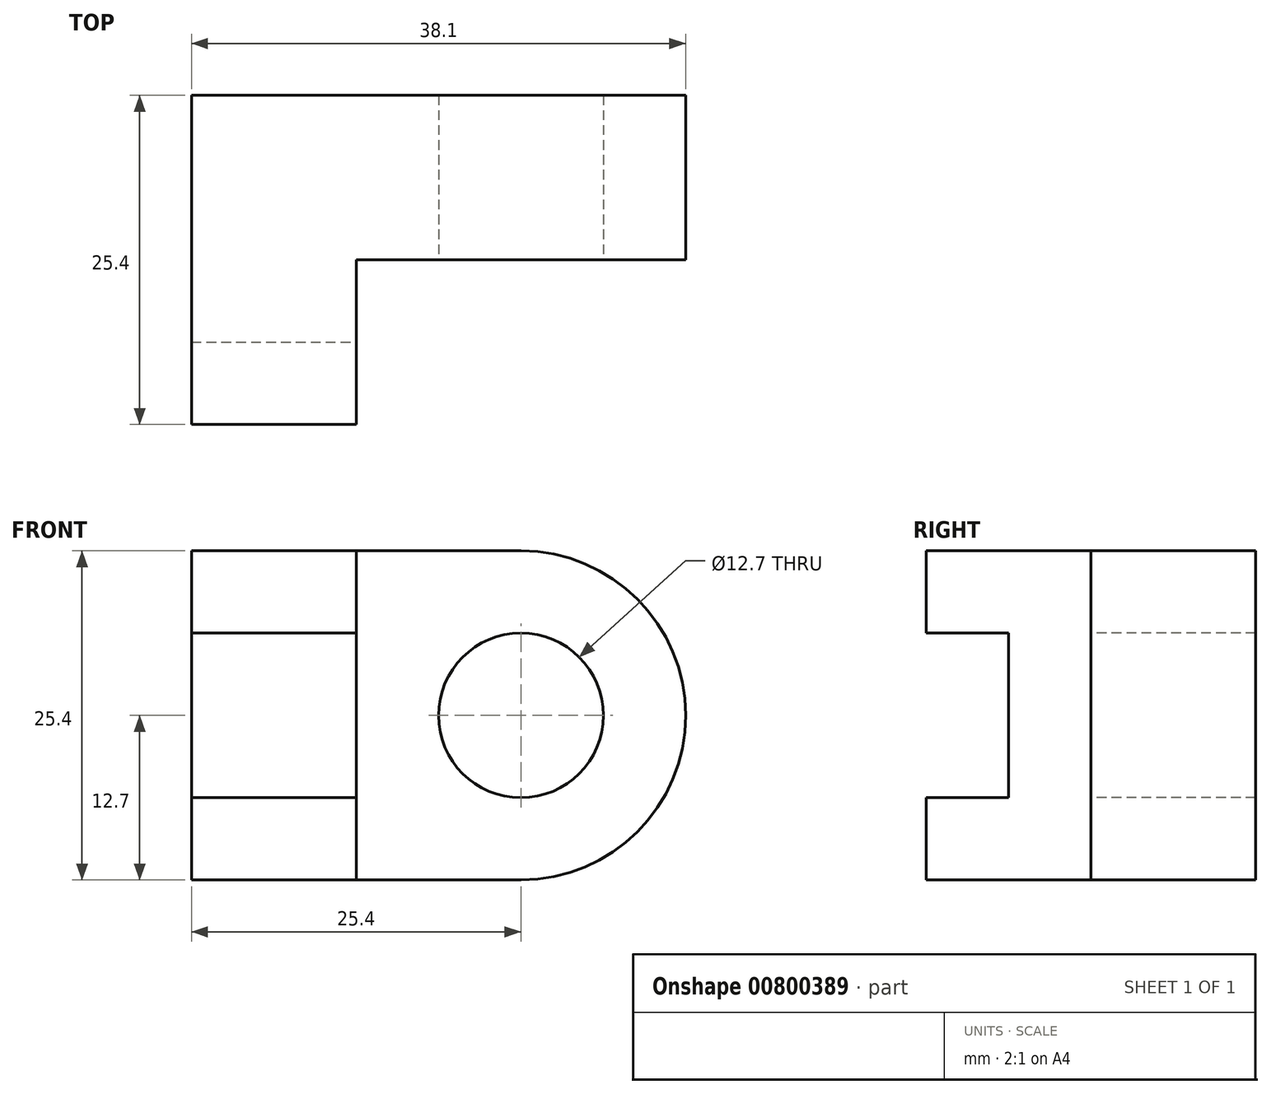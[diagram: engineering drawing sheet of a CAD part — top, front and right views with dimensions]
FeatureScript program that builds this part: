
annotation { "Feature Type Name" : "Feature", "Feature Type Description" : "" }
export const myFeature = defineFeature(function(context is Context, id is Id, definition is map)
    precondition{}
    {
        {
            var Q0;
            Q0=qCreatedBy(makeId("Front.planeOp"),FACE);
            var sketch = newSketch(context, id + "F0", { "sketchPlane" : qUnion([Q0])});
            skLineSegment(sketch, "E0", {"start": v(0, 0) * mm, "end": v(12.7, 0) * mm});
            skLineSegment(sketch, "E1", {"start": v(12.7, 0) * mm, "end": v(12.7, 25.4) * mm});
            skLineSegment(sketch, "E2", {"start": v(12.7, 25.4) * mm, "end": v(0, 25.4) * mm});
            skLineSegment(sketch, "E3", {"start": v(0, 25.4) * mm, "end": v(0, 0) * mm});
            skSolve(sketch);
        }
        {
            var Q0;
            Q0=makeQuery(id+"F0.imprint","IMPRINT",FACE,{"disambiguationData":[TD([[makeQuery(id+"F0.imprint","IMPRINT",EDGE,{"derivedFrom":sQuery(id+"F0.wireOp",EDGE,"E0")}),1.0]])]});
            extrude(context, id + "F1", {"entities" : qUnion([Q0]), "depth" : 25.4 * mm, "offsetDistance" : 25.4 * mm});
        }
        {
            var Q0;
            Q0=makeQuery(id+"F1.opExtrude","CAP_FACE",FACE,{"disambiguationData":[OSD([sQuery(id+"F0.wireOp",EDGE,"E0"),sQuery(id+"F0.wireOp",EDGE,"E1"),sQuery(id+"F0.wireOp",EDGE,"E2"),sQuery(id+"F0.wireOp",EDGE,"E3")])],"isStart":false});
            var sketch = newSketch(context, id + "F2", { "sketchPlane" : qUnion([Q0])});
            skLineSegment(sketch, "E4", {"start": v(0, 0) * mm, "end": v(0, 6.35) * mm});
            skLineSegment(sketch, "E5", {"start": v(0, 6.35) * mm, "end": v(12.7, 6.35) * mm});
            skLineSegment(sketch, "E6", {"start": v(12.7, 6.35) * mm, "end": v(12.7, 19.05) * mm});
            skLineSegment(sketch, "E7", {"start": v(12.7, 19.05) * mm, "end": v(0, 19.05) * mm});
            skSolve(sketch);
        }
        {
            var Q0;
            {var subQ0=sQuery(id+"F2.wireOp",EDGE,"E5");Q0=makeQuery(id+"F2.imprint","IMPRINT",FACE,{"disambiguationData":[TD([[makeQuery(id+"F2.imprint","IMPRINT",EDGE,{"derivedFrom":subQ0}),1.0]])]});}
            extrude(context, id + "F3", {"entities" : qUnion([Q0]), "operationType" : NewBodyOperationType.REMOVE, "oppositeDirection" : true, "depth" : 6.35 * mm, "offsetDistance" : 25.4 * mm});
        }
        {
            var Q0;
            Q0=makeQuery(id+"F1.opExtrude","SWEPT_FACE",FACE,{"disambiguationData":[OSD([sQuery(id+"F0.wireOp",EDGE,"E1")])]});
            var sketch = newSketch(context, id + "F4", { "sketchPlane" : qUnion([Q0])});
            skLineSegment(sketch, "E8", {"start": v(0, 25.4) * mm, "end": v(-12.7, 25.4) * mm, "construction": true});
            skLineSegment(sketch, "E9", {"start": v(-12.7, 25.4) * mm, "end": v(-12.7, 0) * mm});
            skSolve(sketch);
        }
        {
            var Q0;
            Q0 = qSketchRegion(id + "F4", true);
            var Q1;
            {var subQ0=sQuery(id+"F4.wireOp",EDGE,"E9");Q1=makeQuery(id+"F4.imprint","IMPRINT",FACE,{"disambiguationData":[TD([[makeQuery(id+"F4.imprint","IMPRINT",EDGE,{"derivedFrom":subQ0}),1.0]])]});}
            extrude(context, id + "F5", {"entities" : qUnion([Q0, Q1]), "operationType" : NewBodyOperationType.ADD, "depth" : 25.4 * mm, "offsetDistance" : 25.4 * mm});
        }
        {
            var Q0;
            Q0=makeQuery(id+"F5.opExtrude","SWEPT_FACE",FACE,{"disambiguationData":[OSD([sQuery(id+"F4.wireOp",EDGE,"E9")])]});
            var sketch = newSketch(context, id + "F6", { "sketchPlane" : qUnion([Q0])});
            skArc(sketch, "E10", {"start": v(25.4, 0) * mm, "mid": v(38.1, 12.7) * mm, "end": v(25.4, 25.4) * mm});
            skSolve(sketch);
        }
        {
            var Q0;
            {var subQ0=sQuery(id+"F6.wireOp",EDGE,"E10");var subQ1=sQuery(id+"F4.wireOp",EDGE,"E9");var subQ4=makeQuery(id+"F5.opExtrude","CAP_EDGE",EDGE,{"disambiguationData":[OSD([subQ1])],"isStart":false});var subQ5=makeQuery(id+"F6.imprint","INTERSECT",VERTEX,{"derivedFrom":[subQ4,subQ0]});Q0=makeQuery(id+"F6.imprint","IMPRINT",FACE,{"disambiguationData":[TD([[makeQuery(id+"F6.imprint","IMPRINT",EDGE,{"disambiguationData":[TD([[subQ5,-1.0]])],"derivedFrom":subQ0}),-1.0]])]});}
            var Q1;
            {var subQ0=sQuery(id+"F6.wireOp",EDGE,"E10");var subQ1=sQuery(id+"F4.wireOp",EDGE,"E9");var subQ4=makeQuery(id+"F5.opExtrude","CAP_EDGE",EDGE,{"disambiguationData":[OSD([subQ1])],"isStart":false});var subQ5=makeQuery(id+"F6.imprint","INTERSECT",VERTEX,{"derivedFrom":[subQ4,subQ0]});Q1=makeQuery(id+"F6.imprint","IMPRINT",FACE,{"disambiguationData":[TD([[makeQuery(id+"F6.imprint","IMPRINT",EDGE,{"disambiguationData":[TD([[subQ5,1.0]])],"derivedFrom":subQ0}),-1.0]])]});}
            extrude(context, id + "F7", {"entities" : qUnion([Q0, Q1]), "operationType" : NewBodyOperationType.REMOVE, "oppositeDirection" : true, "depth" : 25.4 * mm, "offsetDistance" : 25.4 * mm});
        }
        {
            var Q0;
            Q0=makeQuery(id+"F5.opExtrude","SWEPT_FACE",FACE,{"disambiguationData":[OSD([sQuery(id+"F4.wireOp",EDGE,"E9")])]});
            var sketch = newSketch(context, id + "F8", { "sketchPlane" : qUnion([Q0])});
            skLineSegment(sketch, "E11", {"start": v(12.7, 12.7) * mm, "end": v(25.4, 12.7) * mm, "construction": true});
            skCircle(sketch, "E12", {"center": v(25.4, 12.7) * mm, "radius": 6.35 * mm});
            skSolve(sketch);
        }
        {
            var Q0;
            Q0=makeQuery(id+"F8.imprint","IMPRINT",FACE,{"disambiguationData":[TD([[makeQuery(id+"F8.imprint","IMPRINT",EDGE,{"derivedFrom":sQuery(id+"F8.wireOp",EDGE,"E12")}),1.0]])]});
            extrude(context, id + "F9", {"entities" : qUnion([Q0]), "operationType" : NewBodyOperationType.REMOVE, "endBound" : BoundingType.THROUGH_ALL, "oppositeDirection" : true, "depth" : 25.4 * mm, "offsetDistance" : 25.4 * mm});
        }
    });
